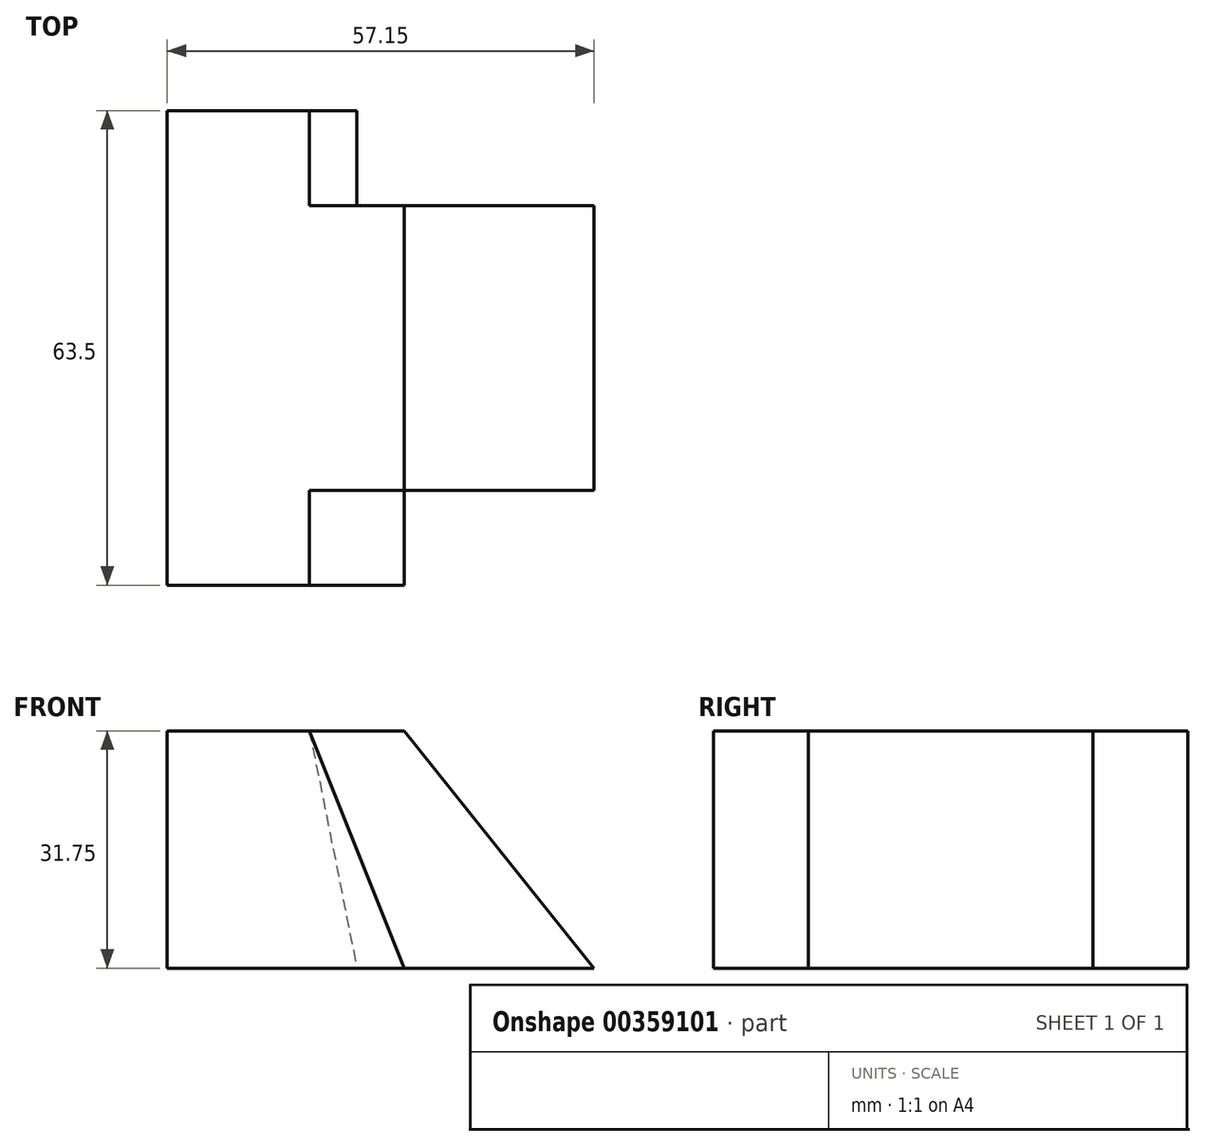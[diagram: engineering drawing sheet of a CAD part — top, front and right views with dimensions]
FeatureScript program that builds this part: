
annotation { "Feature Type Name" : "Feature", "Feature Type Description" : "" }
export const myFeature = defineFeature(function(context is Context, id is Id, definition is map)
    precondition{}
    {
        {
            var Q0;
            Q0=qCreatedBy(makeId("Front.planeOp"),FACE);
            var sketch = newSketch(context, id + "F0", { "sketchPlane" : qUnion([Q0])});
            skLineSegment(sketch, "E0.bottom", {"start": v(-30, 15.97) * mm, "end": v(27.15, 15.97) * mm});
            skLineSegment(sketch, "E0.top", {"start": v(-30, -15.78) * mm, "end": v(27.15, -15.78) * mm});
            skLineSegment(sketch, "E0.left", {"start": v(-30, 15.97) * mm, "end": v(-30, -15.78) * mm});
            skLineSegment(sketch, "E0.right", {"start": v(27.15, 15.97) * mm, "end": v(27.15, -15.78) * mm});
            skSolve(sketch);
        }
        {
            var Q0;
            Q0=makeQuery(id+"F0.imprint","IMPRINT",FACE,{"disambiguationData":[TD([[makeQuery(id+"F0.imprint","IMPRINT",EDGE,{"derivedFrom":sQuery(id+"F0.wireOp",EDGE,"E0.bottom")}),-1.0]])]});
            extrude(context, id + "F1", {"entities" : qUnion([Q0]), "depth" : 38.1 * mm});
        }
        {
            var Q0;
            Q0=makeQuery(id+"F1.opExtrude","CAP_FACE",FACE,{"disambiguationData":[OSD([sQuery(id+"F0.wireOp",EDGE,"E0.bottom"),sQuery(id+"F0.wireOp",EDGE,"E0.top"),sQuery(id+"F0.wireOp",EDGE,"E0.left"),sQuery(id+"F0.wireOp",EDGE,"E0.right")])],"isStart":false});
            var sketch = newSketch(context, id + "F2", { "sketchPlane" : qUnion([Q0])});
            skLineSegment(sketch, "E1", {"start": v(-10.95, 15.97) * mm, "end": v(1.75, -15.78) * mm});
            skSolve(sketch);
        }
        {
            var Q0;
            {var subQ0=sQuery(id+"F2.wireOp",EDGE,"E1");Q0=makeQuery(id+"F2.imprint","IMPRINT",FACE,{"disambiguationData":[TD([[makeQuery(id+"F2.imprint","IMPRINT",EDGE,{"derivedFrom":subQ0}),1.0]])]});}
            extrude(context, id + "F3", {"entities" : qUnion([Q0]), "operationType" : NewBodyOperationType.REMOVE, "oppositeDirection" : true, "depth" : 12.7 * mm});
        }
        {
            var Q0;
            Q0=makeQuery(id+"F1.opExtrude","CAP_FACE",FACE,{"disambiguationData":[OSD([sQuery(id+"F0.wireOp",EDGE,"E0.bottom"),sQuery(id+"F0.wireOp",EDGE,"E0.top"),sQuery(id+"F0.wireOp",EDGE,"E0.left"),sQuery(id+"F0.wireOp",EDGE,"E0.right")])],"isStart":true});
            var sketch = newSketch(context, id + "F4", { "sketchPlane" : qUnion([Q0])});
            skLineSegment(sketch, "E2", {"start": v(10.95, 15.97) * mm, "end": v(4.6, -15.78) * mm});
            skSolve(sketch);
        }
        {
            var Q0;
            Q0 = qSketchRegion(id + "F4", true);
            var Q1;
            {var subQ0=sQuery(id+"F4.wireOp",EDGE,"E2");Q1=makeQuery(id+"F4.imprint","IMPRINT",FACE,{"disambiguationData":[TD([[makeQuery(id+"F4.imprint","IMPRINT",EDGE,{"derivedFrom":subQ0}),-1.0]])]});}
            extrude(context, id + "F5", {"entities" : qUnion([Q0, Q1]), "operationType" : NewBodyOperationType.ADD, "depth" : 25.4 * mm});
        }
        {
            var Q0;
            Q0=makeQuery(id+"F5.opExtrude","CAP_FACE",FACE,{"disambiguationData":[OSD([sQuery(id+"F0.wireOp",EDGE,"E0.bottom"),sQuery(id+"F0.wireOp",EDGE,"E0.top"),sQuery(id+"F0.wireOp",EDGE,"E0.right"),sQuery(id+"F4.wireOp",EDGE,"E2")])],"isStart":false});
            extrude(context, id + "F6", {"entities" : qUnion([Q0]), "operationType" : NewBodyOperationType.REMOVE, "oppositeDirection" : true, "depth" : 12.7 * mm});
        }
        {
            var Q0;
            Q0=makeQuery(id+"F1.opExtrude","CAP_FACE",FACE,{"disambiguationData":[OSD([sQuery(id+"F0.wireOp",EDGE,"E0.bottom"),sQuery(id+"F0.wireOp",EDGE,"E0.top"),sQuery(id+"F0.wireOp",EDGE,"E0.left"),sQuery(id+"F0.wireOp",EDGE,"E0.right")])],"isStart":true});
            extrude(context, id + "F7", {"entities" : qUnion([Q0]), "operationType" : NewBodyOperationType.ADD, "depth" : 25.4 * mm});
        }
        {
            var Q0;
            Q0=makeQuery(id+"F3.boolean.opBoolean","COPY",FACE,{"derivedFrom":makeQuery(id+"F3.opExtrude","CAP_FACE",FACE,{"disambiguationData":[OSD([sQuery(id+"F0.wireOp",EDGE,"E0.bottom"),sQuery(id+"F0.wireOp",EDGE,"E0.top"),sQuery(id+"F0.wireOp",EDGE,"E0.right"),sQuery(id+"F2.wireOp",EDGE,"E1")])],"isStart":false})});
            var sketch = newSketch(context, id + "F8", { "sketchPlane" : qUnion([Q0])});
            skLineSegment(sketch, "E3", {"start": v(14.45, 15.97) * mm, "end": v(27.15, -15.78) * mm});
            skSolve(sketch);
        }
        {
            var Q0;
            Q0 = qSketchRegion(id + "F8", true);
            var Q1;
            {var subQ0=sQuery(id+"F8.wireOp",EDGE,"E3");Q1=makeQuery(id+"F8.imprint","IMPRINT",FACE,{"disambiguationData":[TD([[makeQuery(id+"F8.imprint","IMPRINT",EDGE,{"derivedFrom":subQ0}),1.0]])]});}
            extrude(context, id + "F9", {"entities" : qUnion([Q0, Q1]), "operationType" : NewBodyOperationType.REMOVE, "oppositeDirection" : true, "depth" : 25.4 * mm});
        }
        {
            var Q0;
            Q0=makeQuery(id+"F6.boolean.opBoolean","COPY",FACE,{"derivedFrom":makeQuery(id+"F6.opExtrude","CAP_FACE",FACE,{"disambiguationData":[OSD([sQuery(id+"F0.wireOp",EDGE,"E0.bottom"),sQuery(id+"F0.wireOp",EDGE,"E0.top"),sQuery(id+"F0.wireOp",EDGE,"E0.right"),sQuery(id+"F4.wireOp",EDGE,"E2")])],"isStart":false})});
            var sketch = newSketch(context, id + "F10", { "sketchPlane" : qUnion([Q0])});
            skLineSegment(sketch, "E4", {"start": v(-1.75, 15.97) * mm, "end": v(-27.15, -15.78) * mm});
            skSolve(sketch);
        }
        {
            var Q0;
            {var subQ0=sQuery(id+"F10.wireOp",EDGE,"E4");Q0=makeQuery(id+"F10.imprint","IMPRINT",FACE,{"disambiguationData":[TD([[makeQuery(id+"F10.imprint","IMPRINT",EDGE,{"derivedFrom":subQ0}),-1.0]])]});}
            extrude(context, id + "F11", {"entities" : qUnion([Q0]), "operationType" : NewBodyOperationType.REMOVE, "oppositeDirection" : true, "depth" : 50.8 * mm});
        }
    });
